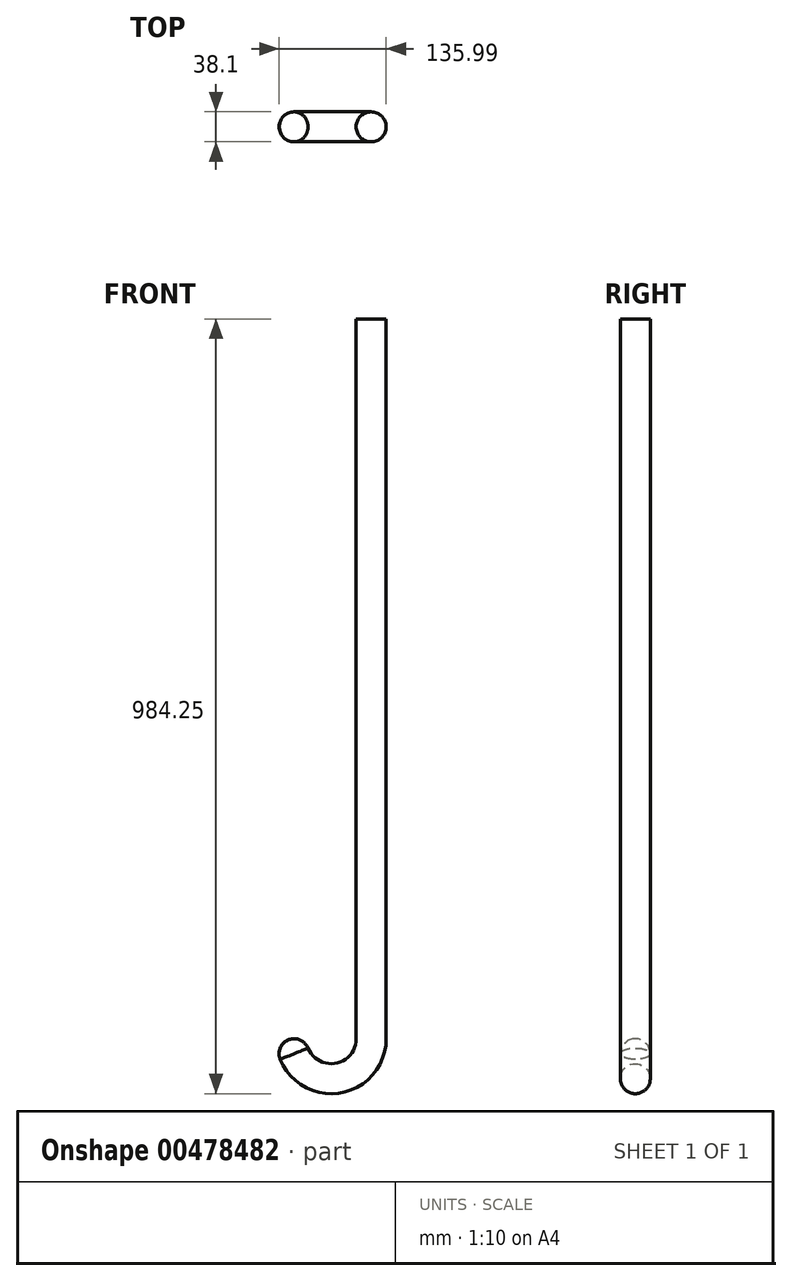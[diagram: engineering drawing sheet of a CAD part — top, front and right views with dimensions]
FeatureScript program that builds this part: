
annotation { "Feature Type Name" : "Feature", "Feature Type Description" : "" }
export const myFeature = defineFeature(function(context is Context, id is Id, definition is map)
    precondition{}
    {
        {
            var Q0;
            Q0=qCreatedBy(makeId("Top.planeOp"),FACE);
            cPlane(context, id + "F0", {"entities" : qUnion([Q0]), "cplaneType" : CPlaneType.OFFSET, "offset" : 381 * mm, "width" : 152.4 * mm, "height" : 152.4 * mm});
        }
        {
            var Q0;
            Q0=qCreatedBy(id+"F0.planeOp",FACE);
            var sketch = newSketch(context, id + "F1", { "sketchPlane" : qUnion([Q0])});
            skCircle(sketch, "E0", {"center": v(0, 0) * mm, "radius": 76.2 * mm});
            skLineSegment(sketch, "E1", {"start": v(0, 76.2) * mm, "end": v(0, -76.2) * mm, "construction": true});
            skLineSegment(sketch, "E2.1.0", {"start": v(53.88, 53.88) * mm, "end": v(-53.88, -53.88) * mm, "construction": true});
            skLineSegment(sketch, "E2.2.0", {"start": v(76.2, 0) * mm, "end": v(-76.2, 0) * mm, "construction": true});
            skLineSegment(sketch, "E2.3.0", {"start": v(53.88, -53.88) * mm, "end": v(-53.88, 53.88) * mm, "construction": true});
            skLineSegment(sketch, "E2.anchor1", {"start": v(0, 0) * mm, "end": v(0, -76.2) * mm, "construction": true});
            skLineSegment(sketch, "E2.anchor2", {"start": v(0, 0) * mm, "end": v(-53.88, 53.88) * mm, "construction": true});
            skSolve(sketch);
        }
        {
            var Q0;
            Q0=qCreatedBy(makeId("Front.planeOp"),FACE);
            var sketch = newSketch(context, id + "F2", { "sketchPlane" : qUnion([Q0])});
            skLineSegment(sketch, "E3", {"start": v(0, 0) * mm, "end": v(0, 381) * mm, "construction": true});
            skSolve(sketch);
        }
        {
            var Q0;
            Q0=qCreatedBy(makeId("Top.planeOp"),FACE);
            var sketch = newSketch(context, id + "F3", { "sketchPlane" : qUnion([Q0])});
            skCircle(sketch, "E4.cCircle", {"center": v(0, 0) * mm, "radius": 422.4 * mm, "construction": true});
            skLineSegment(sketch, "E4.0", {"start": v(323.29, 323.29) * mm, "end": v(457.2, 0) * mm});
            skLineSegment(sketch, "E4.1", {"start": v(457.2, 0) * mm, "end": v(323.29, -323.29) * mm});
            skLineSegment(sketch, "E4.2", {"start": v(323.29, -323.29) * mm, "end": v(0, -457.2) * mm});
            skLineSegment(sketch, "E4.3", {"start": v(0, -457.2) * mm, "end": v(-323.29, -323.29) * mm});
            skLineSegment(sketch, "E4.4", {"start": v(-323.29, -323.29) * mm, "end": v(-457.2, 0) * mm});
            skLineSegment(sketch, "E4.5", {"start": v(-457.2, 0) * mm, "end": v(-323.29, 323.29) * mm});
            skLineSegment(sketch, "E4.6", {"start": v(-323.29, 323.29) * mm, "end": v(0, 457.2) * mm});
            skLineSegment(sketch, "E4.7", {"start": v(0, 457.2) * mm, "end": v(323.29, 323.29) * mm});
            skPoint(sketch, "E4.0.midPoint", {"position": v(390.24, 161.64) * mm});
            skLineSegment(sketch, "E5", {"start": v(0, 457.2) * mm, "end": v(0, -457.2) * mm, "construction": true});
            skSolve(sketch);
        }
        {
            var Q0;
            Q0=qCreatedBy(makeId("Front.planeOp"),FACE);
            var sketch = newSketch(context, id + "F4", { "sketchPlane" : qUnion([Q0])});
            skArc(sketch, "E6", {"start": v(457.2, 0) * mm, "mid": v(345.6, 269.4) * mm, "end": v(76.2, 381) * mm});
            skArc(sketch, "E7.MirrorCS", {"start": v(-457.2, 0) * mm, "mid": v(-345.6, 269.4) * mm, "end": v(-76.2, 381) * mm});
            skSolve(sketch);
        }
        {
            var Q0;
            Q0=qCreatedBy(makeId("Front.planeOp"),FACE);
            var Q1;
            Q1=sQuery(id+"F2.wireOp",EDGE,"E3");
            cPlane(context, id + "F5", {"entities" : qUnion([Q0, Q1]), "cplaneType" : CPlaneType.LINE_ANGLE, "offset" : 25.4 * mm, "angle" : 45 * degree, "width" : 152.4 * mm, "height" : 152.4 * mm});
        }
        {
            var Q0;
            Q0=qCreatedBy(id+"F5.planeOp",FACE);
            var sketch = newSketch(context, id + "F6", { "sketchPlane" : qUnion([Q0])});
            skArc(sketch, "E8", {"start": v(-76.2, 381) * mm, "mid": v(-345.6, 269.4) * mm, "end": v(-457.2, 0) * mm});
            skArc(sketch, "E9.MirrorCS", {"start": v(76.2, 381) * mm, "mid": v(345.6, 269.4) * mm, "end": v(457.2, 0) * mm});
            skSolve(sketch);
        }
        {
            var Q0;
            Q0=qCreatedBy(makeId("Front.planeOp"),FACE);
            var sketch = newSketch(context, id + "F7", { "sketchPlane" : qUnion([Q0])});
            skLineSegment(sketch, "E10", {"start": v(0, 381) * mm, "end": v(0, -533.4) * mm});
            skArc(sketch, "E11", {"start": v(-101.6, -533.4) * mm, "mid": v(-50.8, -584.2) * mm, "end": v(0, -533.4) * mm});
            skSolve(sketch);
        }
        {
            var Q0;
            Q0=qCreatedBy(id+"F0.planeOp",FACE);
            var sketch = newSketch(context, id + "F8", { "sketchPlane" : qUnion([Q0])});
            skCircle(sketch, "E12", {"center": v(0, 0) * mm, "radius": 19.05 * mm});
            skSolve(sketch);
        }
        {
            var Q0;
            Q0=makeQuery(id+"F3.imprint","IMPRINT",FACE,{"disambiguationData":[TD([[makeQuery(id+"F3.imprint","IMPRINT",EDGE,{"derivedFrom":sQuery(id+"F3.wireOp",EDGE,"E4.0")}),-1.0]])]});
            var Q1;
            Q1=sQuery(id+"F1.wireOp",EDGE,"E0");
            var Q2;
            Q2=sQuery(id+"F4.wireOp",EDGE,"E7.MirrorCS");
            var Q3;
            Q3=sQuery(id+"FwEUsNg9eqqxYRy_0.1.F6.wireOp",EDGE,"E8");
            var Q4;
            Q4=sQuery(id+"FwEUsNg9eqqxYRy_0.1.F4.wireOp",EDGE,"E6");
            var Q5;
            Q5=sQuery(id+"F6.wireOp",EDGE,"E8");
            var Q6;
            Q6=sQuery(id+"F4.wireOp",EDGE,"E6");
            var Q7;
            Q7=sQuery(id+"FwEUsNg9eqqxYRy_0.1.F6.wireOp",EDGE,"E9.MirrorCS");
            var Q8;
            Q8=sQuery(id+"FwEUsNg9eqqxYRy_0.1.F4.wireOp",EDGE,"E7.MirrorCS");
            var Q9;
            Q9=sQuery(id+"F6.wireOp",EDGE,"E9.MirrorCS");
            loft(context, id + "F9", {"bodyType" : ToolBodyType.SURFACE, "addGuides" : true, "wireProfilesArray" : [{ "wireProfileEntities" : qUnion([Q0]) }, { "wireProfileEntities" : qUnion([Q1]) }], "guidesArray" : [{ "guideEntities" : qUnion([Q2]), "guideDerivativeType" : LoftGuideDerivativeType.DEFAULT, "guideDerivativeMagnitude" : 1 }, { "guideEntities" : qUnion([Q3]), "guideDerivativeType" : LoftGuideDerivativeType.DEFAULT, "guideDerivativeMagnitude" : 1 }, { "guideEntities" : qUnion([Q4]), "guideDerivativeType" : LoftGuideDerivativeType.DEFAULT, "guideDerivativeMagnitude" : 1 }, { "guideEntities" : qUnion([Q5]), "guideDerivativeType" : LoftGuideDerivativeType.DEFAULT, "guideDerivativeMagnitude" : 1 }, { "guideEntities" : qUnion([Q6]), "guideDerivativeType" : LoftGuideDerivativeType.DEFAULT, "guideDerivativeMagnitude" : 1 }, { "guideEntities" : qUnion([Q7]), "guideDerivativeType" : LoftGuideDerivativeType.DEFAULT, "guideDerivativeMagnitude" : 1 }, { "guideEntities" : qUnion([Q8]), "guideDerivativeType" : LoftGuideDerivativeType.DEFAULT, "guideDerivativeMagnitude" : 1 }, { "guideEntities" : qUnion([Q9]), "guideDerivativeType" : LoftGuideDerivativeType.DEFAULT, "guideDerivativeMagnitude" : 1 }]});
        }
        {
            var Q0;
            Q0=makeQuery(id+"F8.imprint","IMPRINT",FACE,{"disambiguationData":[TD([[makeQuery(id+"F8.imprint","IMPRINT",EDGE,{"derivedFrom":sQuery(id+"F8.wireOp",EDGE,"E12")}),1.0]])]});
            var Q1;
            Q1=sQuery(id+"F7.wireOp",EDGE,"E11");
            var Q2;
            Q2=sQuery(id+"F7.wireOp",EDGE,"E10");
            sweep(context, id + "F10", {"profiles" : qUnion([Q0]), "path" : qUnion([Q1, Q2])});
        }
        {
            var Q0;
            Q0=makeQuery(id+"F10.opSweep","CAP_EDGE",EDGE,{"disambiguationData":[OSD([sQuery(id+"F7.wireOp",VERTEX,"E11.start"),sQuery(id+"F8.wireOp",EDGE,"E12")])],"isStart":false});
            fillet(context, id + "F11", {"entities" : qUnion([Q0]), "radius" : 19.05 * mm, "tangentPropagation" : true, "allowEdgeOverflow" : false});
        }
    });
